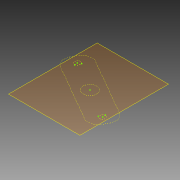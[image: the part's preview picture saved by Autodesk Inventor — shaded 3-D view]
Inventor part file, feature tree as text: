
AUTODESK INVENTOR PART (.ipt)
format: ipt  version: 2015 (Build 190159000, 159)  size: 64,000 bytes
history: native  units: mm
features: plane x1, sketch x1
ambient origin geometry x8: Origin, YZ Plane, XZ Plane, XY Plane, X Axis, Y Axis, Z Axis, Center Point
feature tree (2):
  plane  "Work Plane1"
  sketch  "Sketch1"
